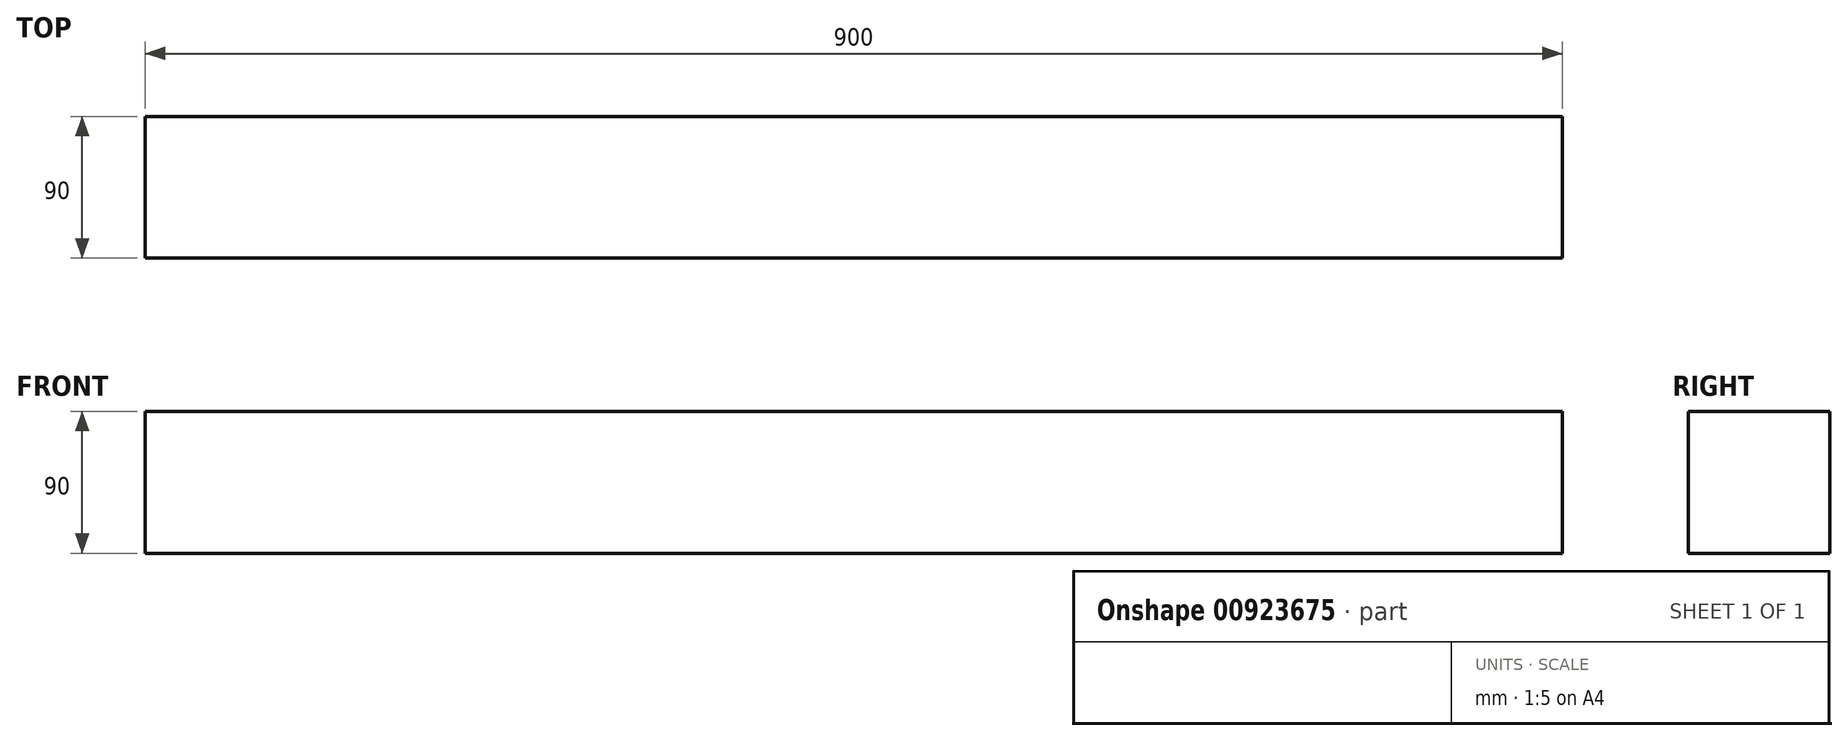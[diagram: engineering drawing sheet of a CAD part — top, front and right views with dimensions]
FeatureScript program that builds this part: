
annotation { "Feature Type Name" : "Feature", "Feature Type Description" : "" }
export const myFeature = defineFeature(function(context is Context, id is Id, definition is map)
    precondition{}
    {
        {
            var Q0;
            Q0=qCreatedBy(makeId("Top.planeOp"),FACE);
            var sketch = newSketch(context, id + "F0", { "sketchPlane" : qUnion([Q0])});
            skLineSegment(sketch, "E0.bottom", {"start": v(-464.01, 89.92) * mm, "end": v(435.99, 89.92) * mm});
            skLineSegment(sketch, "E0.top", {"start": v(-464.01, -0.08) * mm, "end": v(435.99, -0.08) * mm});
            skLineSegment(sketch, "E0.left", {"start": v(-464.01, 89.92) * mm, "end": v(-464.01, -0.08) * mm});
            skLineSegment(sketch, "E0.right", {"start": v(435.99, 89.92) * mm, "end": v(435.99, -0.08) * mm});
            skSolve(sketch);
        }
        {
            var Q0;
            Q0=makeQuery(id+"F0.imprint","IMPRINT",FACE,{"disambiguationData":[TD([[makeQuery(id+"F0.imprint","IMPRINT",EDGE,{"derivedFrom":sQuery(id+"F0.wireOp",EDGE,"E0.bottom")}),-1.0]])]});
            extrude(context, id + "F1", {"entities" : qUnion([Q0]), "depth" : 90 * mm, "offsetDistance" : 25 * mm});
        }
    });
